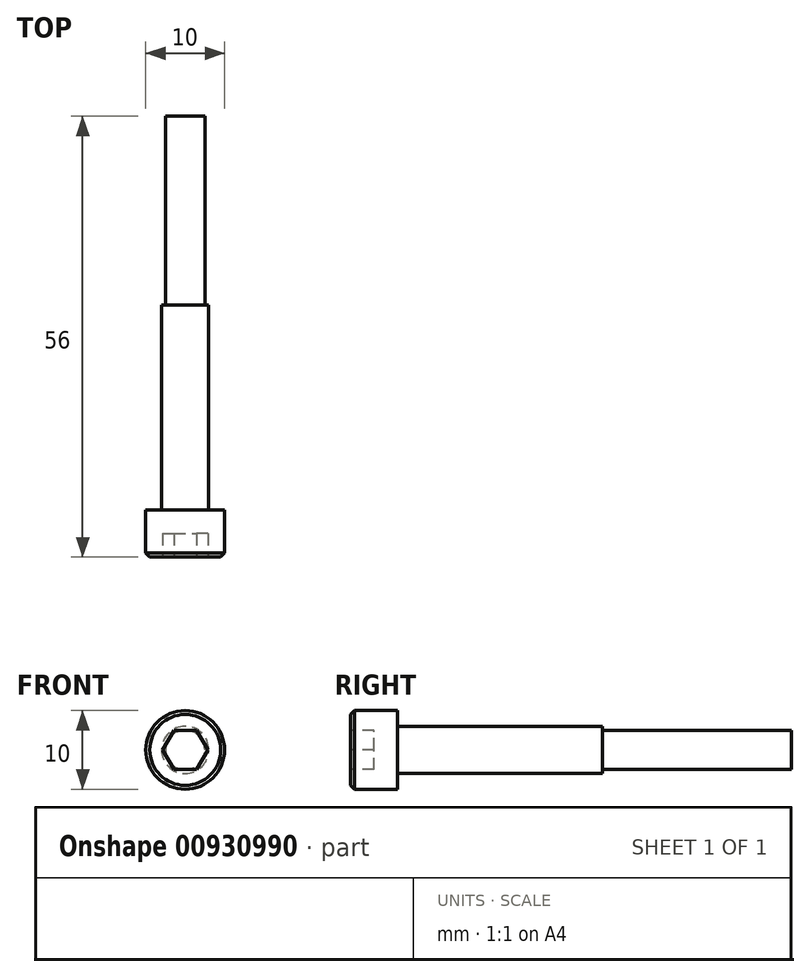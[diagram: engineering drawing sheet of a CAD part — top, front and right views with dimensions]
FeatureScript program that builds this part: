
annotation { "Feature Type Name" : "Feature", "Feature Type Description" : "" }
export const myFeature = defineFeature(function(context is Context, id is Id, definition is map)
    precondition{}
    {
        {
            var Q0;
            Q0=qCreatedBy(makeId("Front.planeOp"),FACE);
            var sketch = newSketch(context, id + "F0", { "sketchPlane" : qUnion([Q0])});
            skCircle(sketch, "E0", {"center": v(0, 0) * mm, "radius": 5 * mm});
            skSolve(sketch);
        }
        {
            var Q0;
            Q0=makeQuery(id+"F0.imprint","IMPRINT",FACE,{"disambiguationData":[TD([[makeQuery(id+"F0.imprint","IMPRINT",EDGE,{"derivedFrom":sQuery(id+"F0.wireOp",EDGE,"E0")}),1.0]])]});
            extrude(context, id + "F1", {"entities" : qUnion([Q0]), "depth" : 6 * mm, "offsetDistance" : 25 * mm});
        }
        {
            var Q0;
            Q0=makeQuery(id+"F1.opExtrude","CAP_FACE",FACE,{"disambiguationData":[OSD([sQuery(id+"F0.wireOp",EDGE,"E0")])],"isStart":true});
            var sketch = newSketch(context, id + "F2", { "sketchPlane" : qUnion([Q0])});
            skCircle(sketch, "E1", {"center": v(0, 0) * mm, "radius": 3 * mm});
            skSolve(sketch);
        }
        {
            var Q0;
            Q0=makeQuery(id+"F2.imprint","IMPRINT",FACE,{"disambiguationData":[TD([[makeQuery(id+"F2.imprint","IMPRINT",EDGE,{"derivedFrom":sQuery(id+"F2.wireOp",EDGE,"E1")}),1.0]])]});
            extrude(context, id + "F3", {"entities" : qUnion([Q0]), "operationType" : NewBodyOperationType.ADD, "depth" : 26 * mm, "offsetDistance" : 25 * mm});
        }
        {
            var Q0;
            Q0=makeQuery(id+"F3.opExtrude","CAP_FACE",FACE,{"disambiguationData":[OSD([sQuery(id+"F2.wireOp",EDGE,"E1")])],"isStart":false});
            var sketch = newSketch(context, id + "F4", { "sketchPlane" : qUnion([Q0])});
            skCircle(sketch, "E2", {"center": v(0, 0) * mm, "radius": 2.5 * mm});
            skSolve(sketch);
        }
        {
            var Q0;
            Q0=makeQuery(id+"F4.imprint","IMPRINT",FACE,{"disambiguationData":[TD([[makeQuery(id+"F4.imprint","IMPRINT",EDGE,{"derivedFrom":sQuery(id+"F4.wireOp",EDGE,"E2")}),1.0]])]});
            extrude(context, id + "F5", {"entities" : qUnion([Q0]), "operationType" : NewBodyOperationType.ADD, "depth" : 24 * mm, "offsetDistance" : 25 * mm});
        }
        {
            var Q0;
            Q0=makeQuery(id+"F1.opExtrude","CAP_FACE",FACE,{"disambiguationData":[OSD([sQuery(id+"F0.wireOp",EDGE,"E0")])],"isStart":false});
            var sketch = newSketch(context, id + "F6", { "sketchPlane" : qUnion([Q0])});
            skCircle(sketch, "E3.cCircle", {"center": v(0, 0) * mm, "radius": 2.5 * mm, "construction": true});
            skLineSegment(sketch, "E3.0", {"start": v(-1.44, 2.5) * mm, "end": v(1.44, 2.5) * mm});
            skLineSegment(sketch, "E3.1", {"start": v(1.44, 2.5) * mm, "end": v(2.89, 0) * mm});
            skLineSegment(sketch, "E3.2", {"start": v(2.89, 0) * mm, "end": v(1.44, -2.5) * mm});
            skLineSegment(sketch, "E3.3", {"start": v(1.44, -2.5) * mm, "end": v(-1.44, -2.5) * mm});
            skLineSegment(sketch, "E3.4", {"start": v(-1.44, -2.5) * mm, "end": v(-2.89, 0) * mm});
            skLineSegment(sketch, "E3.5", {"start": v(-2.89, 0) * mm, "end": v(-1.44, 2.5) * mm});
            skPoint(sketch, "E3.0.midPoint", {"position": v(0, 2.5) * mm});
            skSolve(sketch);
        }
        {
            var Q0;
            Q0=makeQuery(id+"F6.imprint","IMPRINT",FACE,{"disambiguationData":[TD([[makeQuery(id+"F6.imprint","IMPRINT",EDGE,{"derivedFrom":sQuery(id+"F6.wireOp",EDGE,"E3.0")}),-1.0]])]});
            extrude(context, id + "F7", {"entities" : qUnion([Q0]), "operationType" : NewBodyOperationType.REMOVE, "oppositeDirection" : true, "depth" : 3 * mm, "offsetDistance" : 25 * mm});
        }
        {
            var Q0;
            Q0=makeQuery(id+"F1.opExtrude","CAP_EDGE",EDGE,{"disambiguationData":[OSD([sQuery(id+"F0.wireOp",EDGE,"E0")])],"isStart":false});
            chamfer(context, id + "F8", {"entities" : qUnion([Q0]), "width" : 0.5 * mm, "tangentPropagation" : true});
        }
    });
